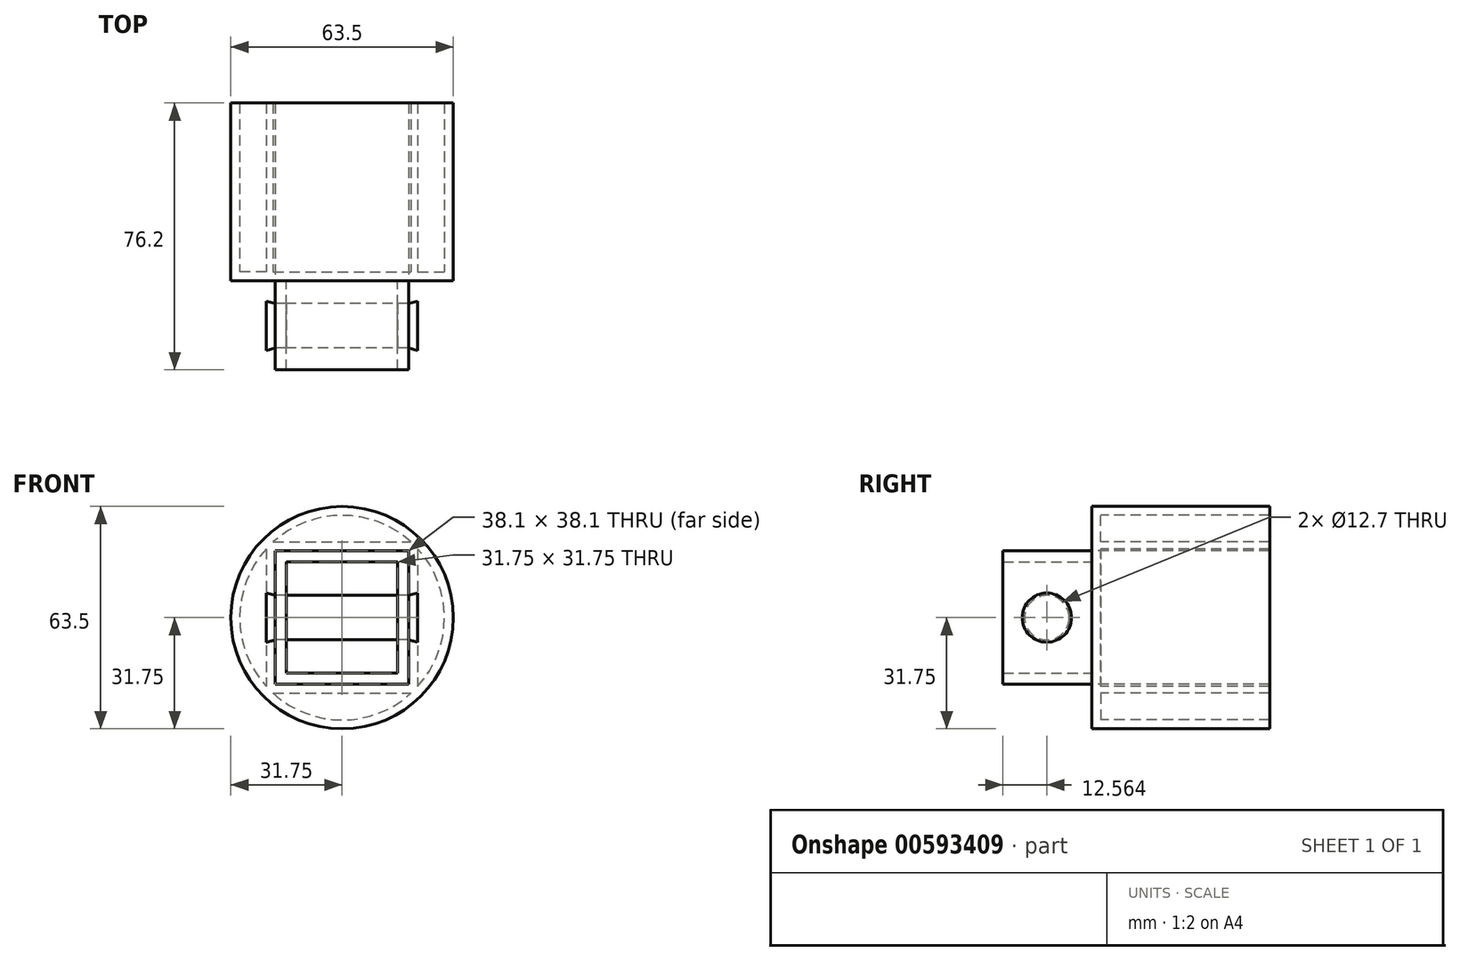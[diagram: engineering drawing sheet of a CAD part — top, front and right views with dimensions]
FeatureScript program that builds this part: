
annotation { "Feature Type Name" : "Feature", "Feature Type Description" : "" }
export const myFeature = defineFeature(function(context is Context, id is Id, definition is map)
    precondition{}
    {
        {
            var Q0;
            Q0=qCreatedBy(makeId("Front.planeOp"),FACE);
            var sketch = newSketch(context, id + "F0", { "sketchPlane" : qUnion([Q0])});
            skCircle(sketch, "E0", {"center": v(0, 0) * mm, "radius": 31.75 * mm});
            skLineSegment(sketch, "E1.bottom", {"start": v(-19.05, 19.05) * mm, "end": v(19.05, 19.05) * mm});
            skLineSegment(sketch, "E1.top", {"start": v(-19.05, -19.05) * mm, "end": v(19.05, -19.05) * mm});
            skLineSegment(sketch, "E1.left", {"start": v(-19.05, 19.05) * mm, "end": v(-19.05, -19.05) * mm});
            skLineSegment(sketch, "E1.right", {"start": v(19.05, 19.05) * mm, "end": v(19.05, -19.05) * mm});
            skLineSegment(sketch, "E2.bottom", {"start": v(-15.87, 15.88) * mm, "end": v(15.88, 15.88) * mm});
            skLineSegment(sketch, "E2.top", {"start": v(-15.88, -15.88) * mm, "end": v(15.87, -15.88) * mm});
            skLineSegment(sketch, "E2.left", {"start": v(-15.87, 15.88) * mm, "end": v(-15.88, -15.88) * mm});
            skLineSegment(sketch, "E2.right", {"start": v(15.88, 15.88) * mm, "end": v(15.87, -15.88) * mm});
            skSolve(sketch);
        }
        {
            var Q0;
            Q0=makeQuery(id+"F0.imprint","IMPRINT",FACE,{"disambiguationData":[TD([[makeQuery(id+"F0.imprint","IMPRINT",EDGE,{"derivedFrom":sQuery(id+"F0.wireOp",EDGE,"E1.bottom")}),-1.0]])]});
            extrude(context, id + "F1", {"entities" : qUnion([Q0]), "depth" : 25.4 * mm, "offsetDistance" : 25.4 * mm});
        }
        {
            var Q0;
            Q0=makeQuery(id+"F0.imprint","IMPRINT",FACE,{"disambiguationData":[TD([[makeQuery(id+"F0.imprint","IMPRINT",EDGE,{"derivedFrom":sQuery(id+"F0.wireOp",EDGE,"E0")}),1.0]])]});
            extrude(context, id + "F2", {"entities" : qUnion([Q0]), "oppositeDirection" : true, "depth" : 50.8 * mm, "offsetDistance" : 25.4 * mm});
        }
        {
            var Q0;
            Q0=makeQuery(id+"F2.opExtrude","CAP_FACE",FACE,{"disambiguationData":[OSD([sQuery(id+"F0.wireOp",EDGE,"E0"),sQuery(id+"F0.wireOp",EDGE,"E1.bottom"),sQuery(id+"F0.wireOp",EDGE,"E1.top"),sQuery(id+"F0.wireOp",EDGE,"E1.left"),sQuery(id+"F0.wireOp",EDGE,"E1.right")])],"isStart":false});
            var Q1;
            Q1=makeQuery(id+"F2.opExtrude","SWEPT_BODY",BODY,{"disambiguationData":[OSD([sQuery(id+"F0.wireOp",EDGE,"E0"),sQuery(id+"F0.wireOp",EDGE,"E1.bottom"),sQuery(id+"F0.wireOp",EDGE,"E1.top"),sQuery(id+"F0.wireOp",EDGE,"E1.left"),sQuery(id+"F0.wireOp",EDGE,"E1.right")])]});
            shell(context, id + "F3", {"entities" : qUnion([Q0]), "parts" : qUnion([Q1]), "thickness" : 2.54 * mm});
        }
        {
            var Q0;
            Q0=qCreatedBy(makeId("Right.planeOp"),FACE);
            var sketch = newSketch(context, id + "F4", { "sketchPlane" : qUnion([Q0])});
            skPoint(sketch, "E3.first.point", {"position": v(0, 0) * mm});
            skLineSegment(sketch, "E4", {"start": v(0, 0) * mm, "end": v(-25.67, 0) * mm});
            skCircle(sketch, "E5", {"center": v(-12.84, 0) * mm, "radius": 6.35 * mm});
            skSolve(sketch);
        }
        {
            var Q0;
            {var subQ0=sQuery(id+"F4.wireOp",EDGE,"E5");var subQ1=sQuery(id+"F4.wireOp",EDGE,"E4");var subQ2=makeQuery(id+"F4.imprint","INTERSECT",VERTEX,{"disambiguationData":[OD(0.0)],"derivedFrom":[subQ1,subQ0]});Q0=makeQuery(id+"F4.imprint","IMPRINT",FACE,{"disambiguationData":[TD([[makeQuery(id+"F4.imprint","IMPRINT",EDGE,{"disambiguationData":[TD([[subQ2,1.0]])],"derivedFrom":subQ1}),-1.0]])]});}
            var Q1;
            {var subQ0=sQuery(id+"F4.wireOp",EDGE,"E5");var subQ1=sQuery(id+"F4.wireOp",EDGE,"E4");var subQ2=makeQuery(id+"F4.imprint","INTERSECT",VERTEX,{"disambiguationData":[OD(0.0)],"derivedFrom":[subQ1,subQ0]});Q1=makeQuery(id+"F4.imprint","IMPRINT",FACE,{"disambiguationData":[TD([[makeQuery(id+"F4.imprint","IMPRINT",EDGE,{"disambiguationData":[TD([[subQ2,1.0]])],"derivedFrom":subQ1}),1.0]])]});}
            extrude(context, id + "F5", {"entities" : qUnion([Q0, Q1]), "operationType" : NewBodyOperationType.REMOVE, "endBound" : BoundingType.SYMMETRIC, "depth" : 50.8 * mm, "offsetDistance" : 25.4 * mm});
        }
        {
            var Q0;
            {var subQ0=sQuery(id+"F4.wireOp",EDGE,"E5");var subQ1=sQuery(id+"F4.wireOp",EDGE,"E4");var subQ2=makeQuery(id+"F4.imprint","INTERSECT",VERTEX,{"disambiguationData":[OD(0.0)],"derivedFrom":[subQ1,subQ0]});Q0=makeQuery(id+"F4.imprint","IMPRINT",FACE,{"disambiguationData":[TD([[makeQuery(id+"F4.imprint","IMPRINT",EDGE,{"disambiguationData":[TD([[subQ2,1.0]])],"derivedFrom":subQ1}),1.0]])]});}
            var Q1;
            {var subQ0=sQuery(id+"F4.wireOp",EDGE,"E5");var subQ1=sQuery(id+"F4.wireOp",EDGE,"E4");var subQ2=makeQuery(id+"F4.imprint","INTERSECT",VERTEX,{"disambiguationData":[OD(0.0)],"derivedFrom":[subQ1,subQ0]});Q1=makeQuery(id+"F4.imprint","IMPRINT",FACE,{"disambiguationData":[TD([[makeQuery(id+"F4.imprint","IMPRINT",EDGE,{"disambiguationData":[TD([[subQ2,1.0]])],"derivedFrom":subQ1}),-1.0]])]});}
            extrude(context, id + "F6", {"entities" : qUnion([Q0, Q1]), "endBound" : BoundingType.SYMMETRIC, "depth" : 38.1 * mm, "offsetDistance" : 25.4 * mm});
        }
        {
            var Q0;
            Q0=makeQuery(id+"F6.opExtrude","CAP_FACE",FACE,{"disambiguationData":[OSD([sQuery(id+"F4.wireOp",EDGE,"E5")])],"isStart":false});
            extrude(context, id + "F7", {"entities" : qUnion([Q0]), "depth" : 2.54 * mm, "offsetDistance" : 25.4 * mm, "hasDraft" : true, "draftAngle" : 15 * degree});
        }
        {
            var Q0;
            Q0=makeQuery(id+"F6.opExtrude","CAP_FACE",FACE,{"disambiguationData":[OSD([sQuery(id+"F4.wireOp",EDGE,"E5")])],"isStart":true});
            extrude(context, id + "F8", {"entities" : qUnion([Q0]), "depth" : 2.54 * mm, "offsetDistance" : 25.4 * mm, "hasDraft" : true, "draftAngle" : 15 * degree});
        }
    });
